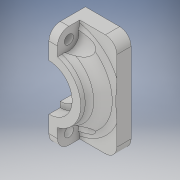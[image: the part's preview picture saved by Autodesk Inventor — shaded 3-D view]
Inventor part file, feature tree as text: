
AUTODESK INVENTOR PART (.ipt)
format: ipt  version: 2018 (Build 220112000, 112)  size: 235,008 bytes
history: native  units: in
note: dims shown in document units (in); Inventor stores cm internally (conversion verified against a paired STEP export)
features: extrude x7, sketch x7, fillet x3, chamfer x1, projected_geometry x1
ambient origin geometry x8: Origin, YZ Plane, XZ Plane, XY Plane, X Axis, Y Axis, Z Axis, Center Point
bodies: Solid1 (feature_tree)
feature tree (19):
  extrude  "Extrusion1"  Depth=1.4213in
  extrude  "Extrusion2"  Depth=0.6299in
  extrude  "Extrusion3"  Depth=0.4921in
  extrude  "Extrusion4"  Depth=0.0709in TaperAngle=0.0deg
  extrude  "Extrusion5"  Depth=0.1181in TaperAngle=0.0deg
  chamfer  "Chamfer1"  Distance=0.1575in
  fillet  "Fillet1"  Radius=0.1181in
  extrude  "Extrusion6"  Depth=0.126in
  fillet  "Fillet2"  Radius=0.1575in
  fillet  "Fillet3"  Radius=0.1575in
  extrude  "Extrusion7"  Depth=0.3937in TaperAngle=0.0deg
  sketch  "Sketch1"  dims[d0=0.6417in d1=1.4213in]
  sketch  "Sketch2"  dims[d2=0.5118in d3=0.6299in]
  sketch  "Sketch3"  dims[d4=0.1969in d5=0.0in d6=0.4921in]
  sketch  "Sketch4"  dims[d7=0.1496in d8=0.0in d9=0.0709in d10=0.0in]
  projected_geometry  "Projected Loop1"
  sketch  "Sketch5"  dims[d11=0.1181in d12=0.1575in d13=0.0in d14=0.1575in d15=0.0in d16=0.1181in]
  sketch  "Sketch6"  dims[d17=0.1575in d18=0.0in d19=0.126in d20=0.1575in d21=0.1575in]
  sketch  "Sketch7"  dims[d22=0.1575in d23=0.1575in d24=0.0in d25=0.1969in d26=0.0787in d27=45.0deg d28=0.1181in d29=0.1575in d30=0.1575in d31=0.2756in d32=0.3937in d33=0.0in]
